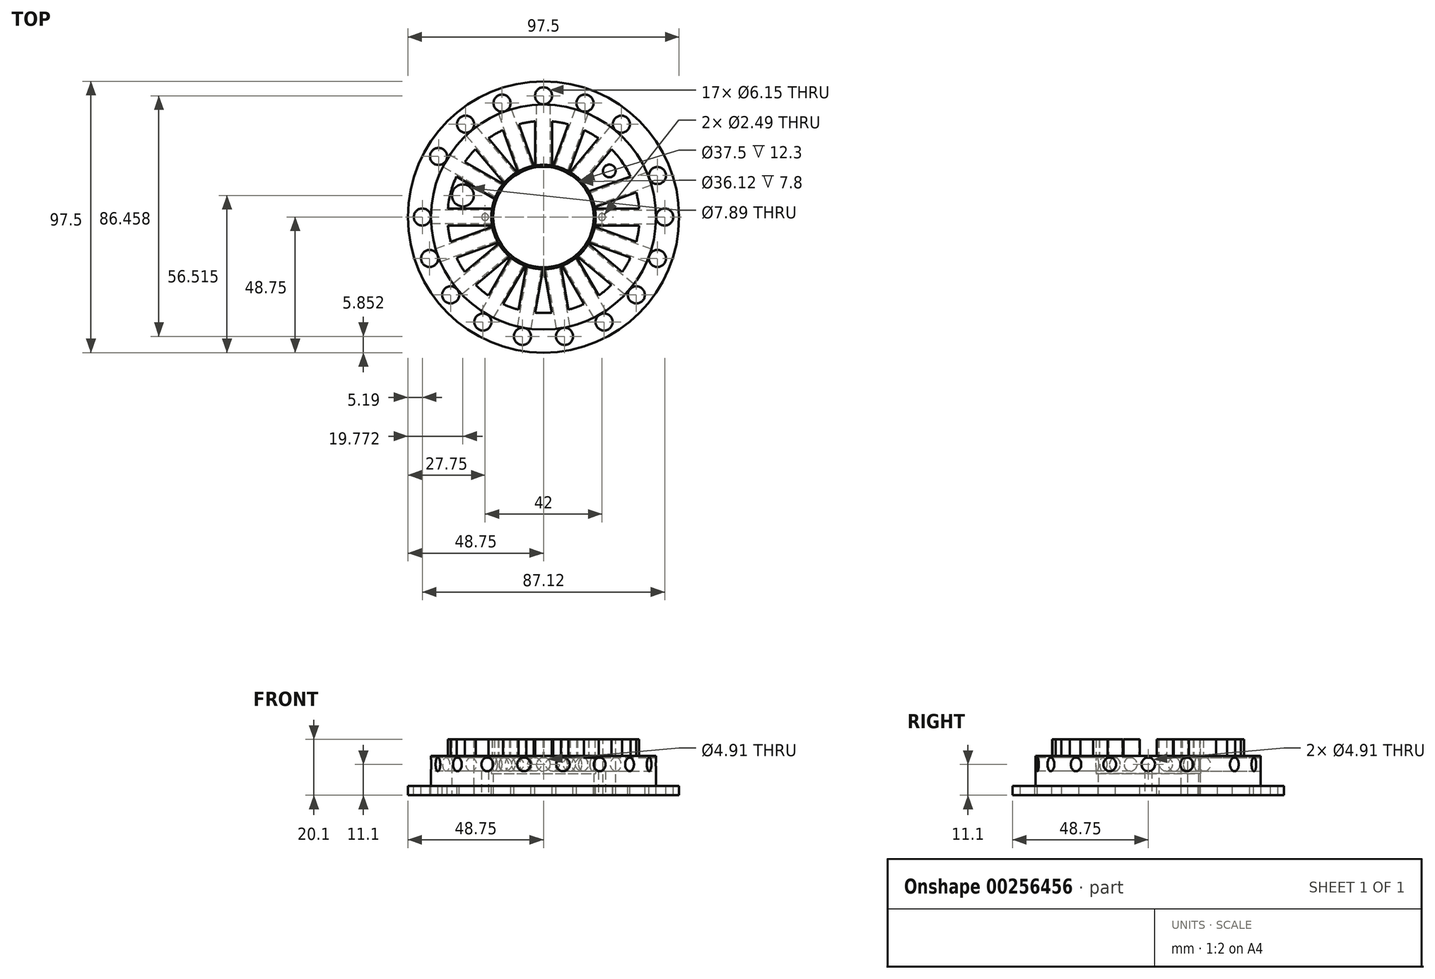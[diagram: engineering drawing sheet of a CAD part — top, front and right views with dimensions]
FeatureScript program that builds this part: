
annotation { "Feature Type Name" : "Feature", "Feature Type Description" : "" }
export const myFeature = defineFeature(function(context is Context, id is Id, definition is map)
    precondition{}
    {
        {
            var Q0;
            Q0=qCreatedBy(makeId("Front.planeOp"),FACE);
            var sketch = newSketch(context, id + "F0", { "sketchPlane" : qUnion([Q0])});
            skLineSegment(sketch, "E0", {"start": v(6.02, 0) * mm, "end": v(16.25, 0) * mm});
            skLineSegment(sketch, "E1", {"start": v(16.25, 0) * mm, "end": v(16.25, 1.1) * mm});
            skLineSegment(sketch, "E2", {"start": v(16.25, 1.1) * mm, "end": v(13.48, 1.1) * mm});
            skLineSegment(sketch, "E3", {"start": v(13.48, 1.1) * mm, "end": v(13.48, 4.7) * mm});
            skLineSegment(sketch, "E4", {"start": v(13.48, 4.7) * mm, "end": v(11.5, 4.7) * mm});
            skLineSegment(sketch, "E5", {"start": v(11.5, 4.7) * mm, "end": v(11.5, 6.7) * mm});
            skLineSegment(sketch, "E6", {"start": v(11.5, 6.7) * mm, "end": v(6.25, 6.7) * mm});
            skLineSegment(sketch, "E7", {"start": v(6.25, 6.7) * mm, "end": v(6.25, 2.6) * mm});
            skLineSegment(sketch, "E8", {"start": v(6.25, 2.6) * mm, "end": v(6.02, 2.6) * mm});
            skLineSegment(sketch, "E9", {"start": v(6.02, 2.6) * mm, "end": v(6.02, 0) * mm});
            skLineSegment(sketch, "E10", {"start": v(0, 0) * mm, "end": v(0, 6.7) * mm, "construction": true});
            skSolve(sketch);
        }
        {
            var Q0;
            Q0=makeQuery(id+"F0.imprint","IMPRINT",FACE,{"disambiguationData":[TD([[makeQuery(id+"F0.imprint","IMPRINT",EDGE,{"derivedFrom":sQuery(id+"F0.wireOp",EDGE,"E0")}),1.0]])]});
            var Q1;
            Q1=sQuery(id+"F0.wireOp",EDGE,"E10");
            revolve(context, id + "F1", {"entities" : qUnion([Q0]), "axis" : qUnion([Q1]), "revolveType" : RevolveType.FULL});
        }
        {
            var Q0;
            Q0=makeQuery(id+"F1.opRevolve","SWEPT_FACE",FACE,{"disambiguationData":[OSD([sQuery(id+"F0.wireOp",EDGE,"E6")])]});
            cPlane(context, id + "F2", {"entities" : qUnion([Q0]), "cplaneType" : CPlaneType.OFFSET, "offset" : 2 * mm, "oppositeDirection" : true, "width" : 150 * mm, "height" : 150 * mm});
        }
        {
            var Q0;
            Q0=qCreatedBy(id+"F2.planeOp",FACE);
            var sketch = newSketch(context, id + "F3", { "sketchPlane" : qUnion([Q0])});
            skLineSegment(sketch, "E11", {"start": v(-15, 1.01) * mm, "end": v(-15, -1.01) * mm});
            skLineSegment(sketch, "E12", {"start": v(-15, -1.01) * mm, "end": v(-5, -1.01) * mm});
            skLineSegment(sketch, "E13", {"start": v(-5, -1.01) * mm, "end": v(-5, 1.01) * mm});
            skLineSegment(sketch, "E14", {"start": v(-5, 1.01) * mm, "end": v(-15, 1.01) * mm});
            skPoint(sketch, "E15.center", {"position": v(0, 0) * mm});
            skLineSegment(sketch, "E16.1.0", {"start": v(-14.44, -4.18) * mm, "end": v(-13.75, -6.08) * mm});
            skLineSegment(sketch, "E16.1.1", {"start": v(-13.75, -6.08) * mm, "end": v(-4.35, -2.66) * mm});
            skLineSegment(sketch, "E16.1.2", {"start": v(-5.05, -0.76) * mm, "end": v(-14.44, -4.18) * mm});
            skLineSegment(sketch, "E16.1.3", {"start": v(-4.35, -2.66) * mm, "end": v(-5.05, -0.76) * mm});
            skLineSegment(sketch, "E16.2.0", {"start": v(-12.14, -8.87) * mm, "end": v(-10.84, -10.42) * mm});
            skLineSegment(sketch, "E16.2.1", {"start": v(-10.84, -10.42) * mm, "end": v(-3.18, -4) * mm});
            skLineSegment(sketch, "E16.2.2", {"start": v(-4.48, -2.44) * mm, "end": v(-12.14, -8.87) * mm});
            skLineSegment(sketch, "E16.2.3", {"start": v(-3.18, -4) * mm, "end": v(-4.48, -2.44) * mm});
            skLineSegment(sketch, "E16.3.0", {"start": v(-8.38, -12.48) * mm, "end": v(-6.62, -13.5) * mm});
            skLineSegment(sketch, "E16.3.1", {"start": v(-6.62, -13.5) * mm, "end": v(-1.62, -4.84) * mm});
            skLineSegment(sketch, "E16.3.2", {"start": v(-3.38, -3.82) * mm, "end": v(-8.38, -12.48) * mm});
            skLineSegment(sketch, "E16.3.3", {"start": v(-1.62, -4.84) * mm, "end": v(-3.38, -3.82) * mm});
            skLineSegment(sketch, "E16.4.0", {"start": v(-3.6, -14.6) * mm, "end": v(-1.6, -14.95) * mm});
            skLineSegment(sketch, "E16.4.1", {"start": v(-1.6, -14.95) * mm, "end": v(0.13, -5.1) * mm});
            skLineSegment(sketch, "E16.4.2", {"start": v(-1.87, -4.75) * mm, "end": v(-3.6, -14.6) * mm});
            skLineSegment(sketch, "E16.4.3", {"start": v(0.13, -5.1) * mm, "end": v(-1.87, -4.75) * mm});
            skLineSegment(sketch, "E16.5.0", {"start": v(1.6, -14.95) * mm, "end": v(3.6, -14.6) * mm});
            skLineSegment(sketch, "E16.5.1", {"start": v(3.6, -14.6) * mm, "end": v(1.87, -4.75) * mm});
            skLineSegment(sketch, "E16.5.2", {"start": v(-0.13, -5.1) * mm, "end": v(1.6, -14.95) * mm});
            skLineSegment(sketch, "E16.5.3", {"start": v(1.87, -4.75) * mm, "end": v(-0.13, -5.1) * mm});
            skLineSegment(sketch, "E16.6.0", {"start": v(6.62, -13.5) * mm, "end": v(8.38, -12.48) * mm});
            skLineSegment(sketch, "E16.6.1", {"start": v(8.38, -12.48) * mm, "end": v(3.38, -3.82) * mm});
            skLineSegment(sketch, "E16.6.2", {"start": v(1.62, -4.84) * mm, "end": v(6.62, -13.5) * mm});
            skLineSegment(sketch, "E16.6.3", {"start": v(3.38, -3.82) * mm, "end": v(1.62, -4.84) * mm});
            skLineSegment(sketch, "E16.7.0", {"start": v(10.84, -10.42) * mm, "end": v(12.14, -8.87) * mm});
            skLineSegment(sketch, "E16.7.1", {"start": v(12.14, -8.87) * mm, "end": v(4.48, -2.44) * mm});
            skLineSegment(sketch, "E16.7.2", {"start": v(3.18, -4) * mm, "end": v(10.84, -10.42) * mm});
            skLineSegment(sketch, "E16.7.3", {"start": v(4.48, -2.44) * mm, "end": v(3.18, -4) * mm});
            skLineSegment(sketch, "E16.8.0", {"start": v(13.75, -6.08) * mm, "end": v(14.44, -4.18) * mm});
            skLineSegment(sketch, "E16.8.1", {"start": v(14.44, -4.18) * mm, "end": v(5.05, -0.76) * mm});
            skLineSegment(sketch, "E16.8.2", {"start": v(4.35, -2.66) * mm, "end": v(13.75, -6.08) * mm});
            skLineSegment(sketch, "E16.8.3", {"start": v(5.05, -0.76) * mm, "end": v(4.35, -2.66) * mm});
            skLineSegment(sketch, "E16.9.0", {"start": v(15, -1.01) * mm, "end": v(15, 1.01) * mm});
            skLineSegment(sketch, "E16.9.1", {"start": v(15, 1.01) * mm, "end": v(5, 1.01) * mm});
            skLineSegment(sketch, "E16.9.2", {"start": v(5, -1.01) * mm, "end": v(15, -1.01) * mm});
            skLineSegment(sketch, "E16.9.3", {"start": v(5, 1.01) * mm, "end": v(5, -1.01) * mm});
            skLineSegment(sketch, "E16.10.0", {"start": v(14.44, 4.18) * mm, "end": v(13.75, 6.08) * mm});
            skLineSegment(sketch, "E16.10.1", {"start": v(13.75, 6.08) * mm, "end": v(4.35, 2.66) * mm});
            skLineSegment(sketch, "E16.10.2", {"start": v(5.05, 0.76) * mm, "end": v(14.44, 4.18) * mm});
            skLineSegment(sketch, "E16.10.3", {"start": v(4.35, 2.66) * mm, "end": v(5.05, 0.76) * mm});
            skLineSegment(sketch, "E16.anchor1", {"start": v(0, 0) * mm, "end": v(-15, -1.01) * mm, "construction": true});
            skLineSegment(sketch, "E16.anchor2", {"start": v(0, 0) * mm, "end": v(13.75, 6.08) * mm, "construction": true});
            skLineSegment(sketch, "E17", {"start": v(-13.5, 6.62) * mm, "end": v(-4.84, 1.62) * mm});
            skLineSegment(sketch, "E18", {"start": v(-4.84, 1.62) * mm, "end": v(-3.82, 3.38) * mm});
            skLineSegment(sketch, "E19", {"start": v(-3.82, 3.38) * mm, "end": v(-12.48, 8.38) * mm});
            skLineSegment(sketch, "E20", {"start": v(-12.48, 8.38) * mm, "end": v(-13.5, 6.62) * mm});
            skLineSegment(sketch, "E21", {"start": v(-13, 7.5) * mm, "end": v(-4.33, 2.5) * mm, "construction": true});
            skLineSegment(sketch, "E22.1.0", {"start": v(-8.87, 12.14) * mm, "end": v(-10.42, 10.84) * mm});
            skLineSegment(sketch, "E22.1.1", {"start": v(-10.42, 10.84) * mm, "end": v(-4, 3.18) * mm});
            skLineSegment(sketch, "E22.1.2", {"start": v(-2.44, 4.48) * mm, "end": v(-8.87, 12.14) * mm});
            skLineSegment(sketch, "E22.1.3", {"start": v(-4, 3.18) * mm, "end": v(-2.44, 4.48) * mm});
            skLineSegment(sketch, "E22.2.0", {"start": v(-4.18, 14.44) * mm, "end": v(-6.08, 13.75) * mm});
            skLineSegment(sketch, "E22.2.1", {"start": v(-6.08, 13.75) * mm, "end": v(-2.66, 4.35) * mm});
            skLineSegment(sketch, "E22.2.2", {"start": v(-0.76, 5.05) * mm, "end": v(-4.18, 14.44) * mm});
            skLineSegment(sketch, "E22.2.3", {"start": v(-2.66, 4.35) * mm, "end": v(-0.76, 5.05) * mm});
            skLineSegment(sketch, "E22.3.0", {"start": v(1.01, 15) * mm, "end": v(-1.01, 15) * mm});
            skLineSegment(sketch, "E22.3.1", {"start": v(-1.01, 15) * mm, "end": v(-1.01, 5) * mm});
            skLineSegment(sketch, "E22.3.2", {"start": v(1.01, 5) * mm, "end": v(1.01, 15) * mm});
            skLineSegment(sketch, "E22.3.3", {"start": v(-1.01, 5) * mm, "end": v(1.01, 5) * mm});
            skLineSegment(sketch, "E22.4.0", {"start": v(6.08, 13.75) * mm, "end": v(4.18, 14.44) * mm});
            skLineSegment(sketch, "E22.4.1", {"start": v(4.18, 14.44) * mm, "end": v(0.76, 5.05) * mm});
            skLineSegment(sketch, "E22.4.2", {"start": v(2.66, 4.35) * mm, "end": v(6.08, 13.75) * mm});
            skLineSegment(sketch, "E22.4.3", {"start": v(0.76, 5.05) * mm, "end": v(2.66, 4.35) * mm});
            skLineSegment(sketch, "E22.5.0", {"start": v(10.42, 10.84) * mm, "end": v(8.87, 12.14) * mm});
            skLineSegment(sketch, "E22.5.1", {"start": v(8.87, 12.14) * mm, "end": v(2.44, 4.48) * mm});
            skLineSegment(sketch, "E22.5.2", {"start": v(4, 3.18) * mm, "end": v(10.42, 10.84) * mm});
            skLineSegment(sketch, "E22.5.3", {"start": v(2.44, 4.48) * mm, "end": v(4, 3.18) * mm});
            skLineSegment(sketch, "E22.anchor1", {"start": v(0, 0) * mm, "end": v(-13.5, 6.62) * mm, "construction": true});
            skLineSegment(sketch, "E22.anchor2", {"start": v(0, 0) * mm, "end": v(8.87, 12.14) * mm, "construction": true});
            skSolve(sketch);
        }
        {
            var Q0;
            Q0=qSketchRegion(id+"F3",true);
            extrude(context, id + "F4", {"entities" : qUnion([Q0]), "operationType" : NewBodyOperationType.REMOVE, "endBound" : BoundingType.THROUGH_ALL, "depth" : 25 * mm});
        }
        {
            var Q0;
            Q0=makeQuery(id+"F1.opRevolve","SWEPT_FACE",FACE,{"disambiguationData":[OSD([sQuery(id+"F0.wireOp",EDGE,"E2")])]});
            var sketch = newSketch(context, id + "F5", { "sketchPlane" : qUnion([Q0])});
            skCircle(sketch, "E23", {"center": v(0, 0) * mm, "radius": 14.52 * mm, "construction": true});
            skCircle(sketch, "E24", {"center": v(-14.52, 0) * mm, "radius": 1.02 * mm});
            skLineSegment(sketch, "E25.anchor1", {"start": v(0, 0) * mm, "end": v(-14.52, 0) * mm, "construction": true});
            skCircle(sketch, "E26.1.0", {"center": v(-12.57, 7.26) * mm, "radius": 1.02 * mm});
            skLineSegment(sketch, "E26.anchor2", {"start": v(0, 0) * mm, "end": v(-12.57, 7.26) * mm, "construction": true});
            skCircle(sketch, "E27.1.0", {"center": v(-13.64, -4.97) * mm, "radius": 1.02 * mm});
            skCircle(sketch, "E27.2.0", {"center": v(-11.12, -9.33) * mm, "radius": 1.02 * mm});
            skCircle(sketch, "E27.3.0", {"center": v(-7.26, -12.57) * mm, "radius": 1.02 * mm});
            skCircle(sketch, "E27.4.0", {"center": v(-2.52, -14.3) * mm, "radius": 1.02 * mm});
            skCircle(sketch, "E27.5.0", {"center": v(2.52, -14.3) * mm, "radius": 1.02 * mm});
            skCircle(sketch, "E27.6.0", {"center": v(7.26, -12.57) * mm, "radius": 1.02 * mm});
            skCircle(sketch, "E27.7.0", {"center": v(11.12, -9.33) * mm, "radius": 1.02 * mm});
            skCircle(sketch, "E27.8.0", {"center": v(13.64, -4.97) * mm, "radius": 1.02 * mm});
            skCircle(sketch, "E27.9.0", {"center": v(14.52, 0) * mm, "radius": 1.02 * mm});
            skCircle(sketch, "E27.10.0", {"center": v(13.64, 4.97) * mm, "radius": 1.02 * mm});
            skLineSegment(sketch, "E27.anchor2", {"start": v(0, 0) * mm, "end": v(13.64, 4.97) * mm, "construction": true});
            skCircle(sketch, "E28.1.0", {"center": v(-9.33, 11.12) * mm, "radius": 1.02 * mm});
            skCircle(sketch, "E28.2.0", {"center": v(-4.97, 13.64) * mm, "radius": 1.02 * mm});
            skCircle(sketch, "E28.3.0", {"center": v(0, 14.52) * mm, "radius": 1.02 * mm});
            skCircle(sketch, "E28.4.0", {"center": v(4.97, 13.64) * mm, "radius": 1.02 * mm});
            skCircle(sketch, "E28.5.0", {"center": v(9.33, 11.12) * mm, "radius": 1.02 * mm});
            skLineSegment(sketch, "E28.anchor2", {"start": v(0, 0) * mm, "end": v(9.33, 11.12) * mm, "construction": true});
            skSolve(sketch);
        }
        {
            var Q0;
            Q0=qSketchRegion(id+"F5",true);
            extrude(context, id + "F6", {"entities" : qUnion([Q0]), "operationType" : NewBodyOperationType.REMOVE, "endBound" : BoundingType.THROUGH_ALL, "oppositeDirection" : true, "depth" : 25 * mm});
        }
        {
            var Q0;
            Q0=makeQuery(id+"F1.opRevolve","SWEPT_FACE",FACE,{"disambiguationData":[OSD([sQuery(id+"F0.wireOp",EDGE,"E0")])]});
            var sketch = newSketch(context, id + "F7", { "sketchPlane" : qUnion([Q0])});
            skCircle(sketch, "E29", {"center": v(-9.66, -2.59) * mm, "radius": 1.31 * mm});
            skLineSegment(sketch, "E30", {"start": v(-9.66, -2.59) * mm, "end": v(0, 0) * mm, "construction": true});
            skSolve(sketch);
        }
        {
            var Q0;
            Q0=makeQuery(id+"F7.imprint","IMPRINT",FACE,{"disambiguationData":[TD([[makeQuery(id+"F7.imprint","IMPRINT",EDGE,{"derivedFrom":sQuery(id+"F7.wireOp",EDGE,"E29")}),1.0]])]});
            extrude(context, id + "F8", {"entities" : qUnion([Q0]), "operationType" : NewBodyOperationType.REMOVE, "endBound" : BoundingType.THROUGH_ALL, "oppositeDirection" : true, "depth" : 25 * mm});
        }
        {
            var Q0;
            Q0=makeQuery(id+"F4.boolean.opBoolean","SPLIT",FACE,{"disambiguationData":[TD([makeQuery(id+"F4.opExtrude","SWEPT_FACE",FACE,{"disambiguationData":[OSD([sQuery(id+"F3.wireOp",EDGE,"E16.10.2")])]})])],"derivedFrom":makeQuery(id+"F1.opRevolve","SWEPT_FACE",FACE,{"disambiguationData":[OSD([sQuery(id+"F0.wireOp",EDGE,"E6")])]})});
            var sketch = newSketch(context, id + "F9", { "sketchPlane" : qUnion([Q0])});
            skCircle(sketch, "E31", {"center": v(7.88, 5.52) * mm, "radius": 0.76 * mm});
            skLineSegment(sketch, "E32", {"start": v(7.88, 5.52) * mm, "end": v(0, 0) * mm, "construction": true});
            skSolve(sketch);
        }
        {
            var Q0;
            Q0=makeQuery(id+"F9.imprint","IMPRINT",FACE,{"disambiguationData":[TD([[makeQuery(id+"F9.imprint","IMPRINT",EDGE,{"derivedFrom":sQuery(id+"F9.wireOp",EDGE,"E31")}),1.0]])]});
            var Q2;
            Q2=makeQuery(id+"F1.opRevolve","SWEPT_FACE",FACE,{"disambiguationData":[OSD([sQuery(id+"F0.wireOp",EDGE,"E0")])]});
            extrude(context, id + "F10", {"entities" : qUnion([Q0]), "operationType" : NewBodyOperationType.REMOVE, "endBound" : BoundingType.UP_TO_SURFACE, "oppositeDirection" : true, "depth" : 1.3 * mm, "endBoundEntityFace" : qUnion([Q2])});
        }
        {
            var Q0;
            Q0=makeQuery(id+"F1.opRevolve","SWEPT_FACE",FACE,{"disambiguationData":[OSD([sQuery(id+"F0.wireOp",EDGE,"E0")])]});
            var sketch = newSketch(context, id + "F11", { "sketchPlane" : qUnion([Q0])});
            skCircle(sketch, "E33", {"center": v(0, 0) * mm, "radius": 7 * mm, "construction": true});
            skCircle(sketch, "E34", {"center": v(-7, 0) * mm, "radius": 0.41 * mm});
            skCircle(sketch, "E35", {"center": v(7, 0) * mm, "radius": 0.41 * mm});
            skSolve(sketch);
        }
        {
            var Q0;
            {Q0=qUnion([makeQuery(id+"F11.imprint","IMPRINT",FACE,{"disambiguationData":[TD([[makeQuery(id+"F11.imprint","IMPRINT",EDGE,{"derivedFrom":sQuery(id+"F11.wireOp",EDGE,"E34")}),1.0]])]}),makeQuery(id+"F11.imprint","IMPRINT",FACE,{"disambiguationData":[TD([[makeQuery(id+"F11.imprint","IMPRINT",EDGE,{"derivedFrom":sQuery(id+"F11.wireOp",EDGE,"E35")}),1.0]])]})]);}
            extrude(context, id + "F12", {"entities" : qUnion([Q0]), "operationType" : NewBodyOperationType.REMOVE, "oppositeDirection" : true, "depth" : 3.7 * mm});
        }
        {
            var Q0;
            Q0=qCreatedBy(id+"F2.planeOp",FACE);
            cPlane(context, id + "F13", {"entities" : qUnion([Q0]), "cplaneType" : CPlaneType.OFFSET, "offset" : 1 * mm, "oppositeDirection" : true, "width" : 150 * mm, "height" : 150 * mm});
        }
        {
            var Q0;
            Q0=qCreatedBy(id+"F13.planeOp",FACE);
            var sketch = newSketch(context, id + "F14", { "sketchPlane" : qUnion([Q0])});
            skLineSegment(sketch, "E36.bottom", {"start": v(-17.2, 0.82) * mm, "end": v(-6.2, 0.82) * mm});
            skLineSegment(sketch, "E36.top", {"start": v(-17.2, 0) * mm, "end": v(-6.2, 0) * mm});
            skLineSegment(sketch, "E36.left", {"start": v(-17.2, 0.82) * mm, "end": v(-17.2, 0) * mm});
            skLineSegment(sketch, "E36.right", {"start": v(-6.2, 0.82) * mm, "end": v(-6.2, 0) * mm});
            skSolve(sketch);
        }
        {
            var Q0;
            Q0=makeQuery(id+"F14.imprint","IMPRINT",FACE,{"disambiguationData":[TD([[makeQuery(id+"F14.imprint","IMPRINT",EDGE,{"derivedFrom":sQuery(id+"F14.wireOp",EDGE,"E36.bottom")}),-1.0]])]});
            var Q1;
            Q1=sQuery(id+"F14.wireOp",EDGE,"E36.top");
            revolve(context, id + "F15", {"entities" : qUnion([Q0]), "axis" : qUnion([Q1]), "revolveType" : RevolveType.FULL});
        }
        {
            var Q0;
            Q0=makeQuery(id+"F15.opRevolve","SWEPT_BODY",BODY,{"disambiguationData":[OSD([sQuery(id+"F14.wireOp",EDGE,"E36.bottom"),sQuery(id+"F14.wireOp",EDGE,"E36.top"),sQuery(id+"F14.wireOp",EDGE,"E36.left"),sQuery(id+"F14.wireOp",EDGE,"E36.right")])]});
            var Q1;
            Q1=sQuery(id+"F0.wireOp",EDGE,"E10");
            circularPattern(context, id + "F16", {"entities" : qUnion([Q0]), "axis" : qUnion([Q1]), "angle" : 20 * degree, "instanceCount" : round(11), "computeTransformsWithoutBuiltin" : true});
        }
        {
            var Q0;
            Q0=makeQuery(id+"F15.opRevolve","SWEPT_BODY",BODY,{"disambiguationData":[OSD([sQuery(id+"F14.wireOp",EDGE,"E36.bottom"),sQuery(id+"F14.wireOp",EDGE,"E36.top"),sQuery(id+"F14.wireOp",EDGE,"E36.left"),sQuery(id+"F14.wireOp",EDGE,"E36.right")])]});
            var Q1;
            Q1=sQuery(id+"F0.wireOp",EDGE,"E10");
            transform(context, id + "F17", {"entities" : qUnion([Q0]), "transformType" : TransformType.ROTATION, "transformAxis" : qUnion([Q1]), "angle" : 30 * degree, "oppositeDirection" : true, "makeCopy" : true});
        }
        {
            var Q0;
            Q0=makeQuery(id+"F17.opPattern","COPY",FACE,{"derivedFrom":makeQuery(id+"F15.opRevolve","SWEPT_FACE",FACE,{"disambiguationData":[OSD([sQuery(id+"F14.wireOp",EDGE,"E36.bottom")])]}),"instanceName":"1"});
            var Q1;
            Q1=makeQuery(id+"F17.opPattern","COPY",BODY,{"derivedFrom":makeQuery(id+"F15.opRevolve","SWEPT_BODY",BODY,{"disambiguationData":[OSD([sQuery(id+"F14.wireOp",EDGE,"E36.bottom"),sQuery(id+"F14.wireOp",EDGE,"E36.top"),sQuery(id+"F14.wireOp",EDGE,"E36.left"),sQuery(id+"F14.wireOp",EDGE,"E36.right")])]}),"instanceName":"1"});
            var Q2;
            Q2=sQuery(id+"F0.wireOp",EDGE,"E10");
            circularPattern(context, id + "F18", {"entities" : qUnion([Q1]), "axis" : qUnion([Q2]), "angle" : 20 * degree, "instanceCount" : round(6), "oppositeDirection" : true, "computeTransformsWithoutBuiltin" : true});
        }
        {
            var Q0;
            Q0=makeQuery(id+"F15.opRevolve","SWEPT_BODY",BODY,{"disambiguationData":[OSD([sQuery(id+"F14.wireOp",EDGE,"E36.bottom"),sQuery(id+"F14.wireOp",EDGE,"E36.top"),sQuery(id+"F14.wireOp",EDGE,"E36.left"),sQuery(id+"F14.wireOp",EDGE,"E36.right")])]});
            var Q1;
            Q1=makeQuery(id+"F16.opPattern","COPY",BODY,{"derivedFrom":makeQuery(id+"F15.opRevolve","SWEPT_BODY",BODY,{"disambiguationData":[OSD([sQuery(id+"F14.wireOp",EDGE,"E36.bottom"),sQuery(id+"F14.wireOp",EDGE,"E36.top"),sQuery(id+"F14.wireOp",EDGE,"E36.left"),sQuery(id+"F14.wireOp",EDGE,"E36.right")])]}),"instanceName":"1"});
            var Q2;
            Q2=makeQuery(id+"F16.opPattern","COPY",BODY,{"derivedFrom":makeQuery(id+"F15.opRevolve","SWEPT_BODY",BODY,{"disambiguationData":[OSD([sQuery(id+"F14.wireOp",EDGE,"E36.bottom"),sQuery(id+"F14.wireOp",EDGE,"E36.top"),sQuery(id+"F14.wireOp",EDGE,"E36.left"),sQuery(id+"F14.wireOp",EDGE,"E36.right")])]}),"instanceName":"2"});
            var Q3;
            Q3=makeQuery(id+"F16.opPattern","COPY",BODY,{"derivedFrom":makeQuery(id+"F15.opRevolve","SWEPT_BODY",BODY,{"disambiguationData":[OSD([sQuery(id+"F14.wireOp",EDGE,"E36.bottom"),sQuery(id+"F14.wireOp",EDGE,"E36.top"),sQuery(id+"F14.wireOp",EDGE,"E36.left"),sQuery(id+"F14.wireOp",EDGE,"E36.right")])]}),"instanceName":"3"});
            var Q4;
            Q4=makeQuery(id+"F16.opPattern","COPY",BODY,{"derivedFrom":makeQuery(id+"F15.opRevolve","SWEPT_BODY",BODY,{"disambiguationData":[OSD([sQuery(id+"F14.wireOp",EDGE,"E36.bottom"),sQuery(id+"F14.wireOp",EDGE,"E36.top"),sQuery(id+"F14.wireOp",EDGE,"E36.left"),sQuery(id+"F14.wireOp",EDGE,"E36.right")])]}),"instanceName":"4"});
            var Q5;
            Q5=makeQuery(id+"F16.opPattern","COPY",BODY,{"derivedFrom":makeQuery(id+"F15.opRevolve","SWEPT_BODY",BODY,{"disambiguationData":[OSD([sQuery(id+"F14.wireOp",EDGE,"E36.bottom"),sQuery(id+"F14.wireOp",EDGE,"E36.top"),sQuery(id+"F14.wireOp",EDGE,"E36.left"),sQuery(id+"F14.wireOp",EDGE,"E36.right")])]}),"instanceName":"5"});
            var Q6;
            Q6=makeQuery(id+"F16.opPattern","COPY",BODY,{"derivedFrom":makeQuery(id+"F15.opRevolve","SWEPT_BODY",BODY,{"disambiguationData":[OSD([sQuery(id+"F14.wireOp",EDGE,"E36.bottom"),sQuery(id+"F14.wireOp",EDGE,"E36.top"),sQuery(id+"F14.wireOp",EDGE,"E36.left"),sQuery(id+"F14.wireOp",EDGE,"E36.right")])]}),"instanceName":"6"});
            var Q7;
            Q7=makeQuery(id+"F16.opPattern","COPY",BODY,{"derivedFrom":makeQuery(id+"F15.opRevolve","SWEPT_BODY",BODY,{"disambiguationData":[OSD([sQuery(id+"F14.wireOp",EDGE,"E36.bottom"),sQuery(id+"F14.wireOp",EDGE,"E36.top"),sQuery(id+"F14.wireOp",EDGE,"E36.left"),sQuery(id+"F14.wireOp",EDGE,"E36.right")])]}),"instanceName":"7"});
            var Q8;
            Q8=makeQuery(id+"F16.opPattern","COPY",BODY,{"derivedFrom":makeQuery(id+"F15.opRevolve","SWEPT_BODY",BODY,{"disambiguationData":[OSD([sQuery(id+"F14.wireOp",EDGE,"E36.bottom"),sQuery(id+"F14.wireOp",EDGE,"E36.top"),sQuery(id+"F14.wireOp",EDGE,"E36.left"),sQuery(id+"F14.wireOp",EDGE,"E36.right")])]}),"instanceName":"8"});
            var Q9;
            Q9=makeQuery(id+"F16.opPattern","COPY",BODY,{"derivedFrom":makeQuery(id+"F15.opRevolve","SWEPT_BODY",BODY,{"disambiguationData":[OSD([sQuery(id+"F14.wireOp",EDGE,"E36.bottom"),sQuery(id+"F14.wireOp",EDGE,"E36.top"),sQuery(id+"F14.wireOp",EDGE,"E36.left"),sQuery(id+"F14.wireOp",EDGE,"E36.right")])]}),"instanceName":"9"});
            var Q10;
            Q10=makeQuery(id+"F16.opPattern","COPY",BODY,{"derivedFrom":makeQuery(id+"F15.opRevolve","SWEPT_BODY",BODY,{"disambiguationData":[OSD([sQuery(id+"F14.wireOp",EDGE,"E36.bottom"),sQuery(id+"F14.wireOp",EDGE,"E36.top"),sQuery(id+"F14.wireOp",EDGE,"E36.left"),sQuery(id+"F14.wireOp",EDGE,"E36.right")])]}),"instanceName":"10"});
            var Q11;
            Q11=makeQuery(id+"F17.opPattern","COPY",BODY,{"derivedFrom":makeQuery(id+"F15.opRevolve","SWEPT_BODY",BODY,{"disambiguationData":[OSD([sQuery(id+"F14.wireOp",EDGE,"E36.bottom"),sQuery(id+"F14.wireOp",EDGE,"E36.top"),sQuery(id+"F14.wireOp",EDGE,"E36.left"),sQuery(id+"F14.wireOp",EDGE,"E36.right")])]}),"instanceName":"1"});
            var Q12;
            Q12=makeQuery(id+"F18.opPattern","COPY",BODY,{"derivedFrom":makeQuery(id+"F17.opPattern","COPY",BODY,{"derivedFrom":makeQuery(id+"F15.opRevolve","SWEPT_BODY",BODY,{"disambiguationData":[OSD([sQuery(id+"F14.wireOp",EDGE,"E36.bottom"),sQuery(id+"F14.wireOp",EDGE,"E36.top"),sQuery(id+"F14.wireOp",EDGE,"E36.left"),sQuery(id+"F14.wireOp",EDGE,"E36.right")])]}),"instanceName":"1"}),"instanceName":"1"});
            var Q13;
            Q13=makeQuery(id+"F18.opPattern","COPY",BODY,{"derivedFrom":makeQuery(id+"F17.opPattern","COPY",BODY,{"derivedFrom":makeQuery(id+"F15.opRevolve","SWEPT_BODY",BODY,{"disambiguationData":[OSD([sQuery(id+"F14.wireOp",EDGE,"E36.bottom"),sQuery(id+"F14.wireOp",EDGE,"E36.top"),sQuery(id+"F14.wireOp",EDGE,"E36.left"),sQuery(id+"F14.wireOp",EDGE,"E36.right")])]}),"instanceName":"1"}),"instanceName":"2"});
            var Q14;
            Q14=makeQuery(id+"F18.opPattern","COPY",BODY,{"derivedFrom":makeQuery(id+"F17.opPattern","COPY",BODY,{"derivedFrom":makeQuery(id+"F15.opRevolve","SWEPT_BODY",BODY,{"disambiguationData":[OSD([sQuery(id+"F14.wireOp",EDGE,"E36.bottom"),sQuery(id+"F14.wireOp",EDGE,"E36.top"),sQuery(id+"F14.wireOp",EDGE,"E36.left"),sQuery(id+"F14.wireOp",EDGE,"E36.right")])]}),"instanceName":"1"}),"instanceName":"3"});
            var Q15;
            Q15=makeQuery(id+"F18.opPattern","COPY",BODY,{"derivedFrom":makeQuery(id+"F17.opPattern","COPY",BODY,{"derivedFrom":makeQuery(id+"F15.opRevolve","SWEPT_BODY",BODY,{"disambiguationData":[OSD([sQuery(id+"F14.wireOp",EDGE,"E36.bottom"),sQuery(id+"F14.wireOp",EDGE,"E36.top"),sQuery(id+"F14.wireOp",EDGE,"E36.left"),sQuery(id+"F14.wireOp",EDGE,"E36.right")])]}),"instanceName":"1"}),"instanceName":"4"});
            var Q16;
            Q16=makeQuery(id+"F18.opPattern","COPY",BODY,{"derivedFrom":makeQuery(id+"F17.opPattern","COPY",BODY,{"derivedFrom":makeQuery(id+"F15.opRevolve","SWEPT_BODY",BODY,{"disambiguationData":[OSD([sQuery(id+"F14.wireOp",EDGE,"E36.bottom"),sQuery(id+"F14.wireOp",EDGE,"E36.top"),sQuery(id+"F14.wireOp",EDGE,"E36.left"),sQuery(id+"F14.wireOp",EDGE,"E36.right")])]}),"instanceName":"1"}),"instanceName":"5"});
            var Q17;
            Q17=makeQuery(id+"F1.opRevolve","SWEPT_BODY",BODY,{"disambiguationData":[OSD([sQuery(id+"F0.wireOp",EDGE,"E0"),sQuery(id+"F0.wireOp",EDGE,"E1"),sQuery(id+"F0.wireOp",EDGE,"E2"),sQuery(id+"F0.wireOp",EDGE,"E3"),sQuery(id+"F0.wireOp",EDGE,"E4"),sQuery(id+"F0.wireOp",EDGE,"E5"),sQuery(id+"F0.wireOp",EDGE,"E6"),sQuery(id+"F0.wireOp",EDGE,"E7"),sQuery(id+"F0.wireOp",EDGE,"E8"),sQuery(id+"F0.wireOp",EDGE,"E9")])]});
            booleanBodies(context, id + "F19", {"operationType" : BooleanOperationType.SUBTRACTION, "tools" : qUnion([Q0, Q1, Q2, Q3, Q4, Q5, Q6, Q7, Q8, Q9, Q10, Q11, Q12, Q13, Q14, Q15, Q16]), "targets" : qUnion([Q17])});
        }
        {
            var Q0;
            Q0=makeQuery(id+"F4.boolean.opBoolean","MERGE",FACE,{"derivedFrom":[makeQuery(id+"F1.opRevolve","SWEPT_FACE",FACE,{"disambiguationData":[OSD([sQuery(id+"F0.wireOp",EDGE,"E4")])]}),makeQuery(id+"F4.opExtrude","CAP_FACE",FACE,{"disambiguationData":[OSD([sQuery(id+"F3.wireOp",EDGE,"E11"),sQuery(id+"F3.wireOp",EDGE,"E12"),sQuery(id+"F3.wireOp",EDGE,"E13"),sQuery(id+"F3.wireOp",EDGE,"E14"),sQuery(id+"F3.wireOp",EDGE,"E16.1.0"),sQuery(id+"F3.wireOp",EDGE,"E16.1.1"),sQuery(id+"F3.wireOp",EDGE,"E16.1.2"),sQuery(id+"F3.wireOp",EDGE,"E16.1.3"),sQuery(id+"F3.wireOp",EDGE,"E16.2.0"),sQuery(id+"F3.wireOp",EDGE,"E16.2.1"),sQuery(id+"F3.wireOp",EDGE,"E16.2.2"),sQuery(id+"F3.wireOp",EDGE,"E16.2.3"),sQuery(id+"F3.wireOp",EDGE,"E16.3.0"),sQuery(id+"F3.wireOp",EDGE,"E16.3.1"),sQuery(id+"F3.wireOp",EDGE,"E16.3.2"),sQuery(id+"F3.wireOp",EDGE,"E16.3.3"),sQuery(id+"F3.wireOp",EDGE,"E16.4.0"),sQuery(id+"F3.wireOp",EDGE,"E16.4.1"),sQuery(id+"F3.wireOp",EDGE,"E16.4.2"),sQuery(id+"F3.wireOp",EDGE,"E16.4.3"),sQuery(id+"F3.wireOp",EDGE,"E16.5.0"),sQuery(id+"F3.wireOp",EDGE,"E16.5.1"),sQuery(id+"F3.wireOp",EDGE,"E16.5.2"),sQuery(id+"F3.wireOp",EDGE,"E16.5.3"),sQuery(id+"F3.wireOp",EDGE,"E16.6.0"),sQuery(id+"F3.wireOp",EDGE,"E16.6.1"),sQuery(id+"F3.wireOp",EDGE,"E16.6.2"),sQuery(id+"F3.wireOp",EDGE,"E16.6.3"),sQuery(id+"F3.wireOp",EDGE,"E16.7.0"),sQuery(id+"F3.wireOp",EDGE,"E16.7.1"),sQuery(id+"F3.wireOp",EDGE,"E16.7.2"),sQuery(id+"F3.wireOp",EDGE,"E16.7.3"),sQuery(id+"F3.wireOp",EDGE,"E16.8.0"),sQuery(id+"F3.wireOp",EDGE,"E16.8.1"),sQuery(id+"F3.wireOp",EDGE,"E16.8.2"),sQuery(id+"F3.wireOp",EDGE,"E16.8.3"),sQuery(id+"F3.wireOp",EDGE,"E16.9.0"),sQuery(id+"F3.wireOp",EDGE,"E16.9.1"),sQuery(id+"F3.wireOp",EDGE,"E16.9.2"),sQuery(id+"F3.wireOp",EDGE,"E16.9.3"),sQuery(id+"F3.wireOp",EDGE,"E16.10.0"),sQuery(id+"F3.wireOp",EDGE,"E16.10.1"),sQuery(id+"F3.wireOp",EDGE,"E16.10.2"),sQuery(id+"F3.wireOp",EDGE,"E16.10.3")])],"isStart":true}),makeQuery(id+"F4.opExtrude","CAP_FACE",FACE,{"disambiguationData":[OSD([sQuery(id+"F3.wireOp",EDGE,"E17"),sQuery(id+"F3.wireOp",EDGE,"E18"),sQuery(id+"F3.wireOp",EDGE,"E19"),sQuery(id+"F3.wireOp",EDGE,"E20"),sQuery(id+"F3.wireOp",EDGE,"E22.1.0"),sQuery(id+"F3.wireOp",EDGE,"E22.1.1"),sQuery(id+"F3.wireOp",EDGE,"E22.1.2"),sQuery(id+"F3.wireOp",EDGE,"E22.1.3"),sQuery(id+"F3.wireOp",EDGE,"E22.2.0"),sQuery(id+"F3.wireOp",EDGE,"E22.2.1"),sQuery(id+"F3.wireOp",EDGE,"E22.2.2"),sQuery(id+"F3.wireOp",EDGE,"E22.2.3"),sQuery(id+"F3.wireOp",EDGE,"E22.3.0"),sQuery(id+"F3.wireOp",EDGE,"E22.3.1"),sQuery(id+"F3.wireOp",EDGE,"E22.3.2"),sQuery(id+"F3.wireOp",EDGE,"E22.3.3"),sQuery(id+"F3.wireOp",EDGE,"E22.4.0"),sQuery(id+"F3.wireOp",EDGE,"E22.4.1"),sQuery(id+"F3.wireOp",EDGE,"E22.4.2"),sQuery(id+"F3.wireOp",EDGE,"E22.4.3"),sQuery(id+"F3.wireOp",EDGE,"E22.5.0"),sQuery(id+"F3.wireOp",EDGE,"E22.5.1"),sQuery(id+"F3.wireOp",EDGE,"E22.5.2"),sQuery(id+"F3.wireOp",EDGE,"E22.5.3")])],"isStart":true})]});
            cPlane(context, id + "F20", {"entities" : qUnion([Q0]), "cplaneType" : CPlaneType.OFFSET, "offset" : 4 * mm, "oppositeDirection" : true, "width" : 150 * mm, "height" : 150 * mm});
        }
        {
            var Q0;
            Q0=qCreatedBy(id+"F20.planeOp",FACE);
            var sketch = newSketch(context, id + "F21", { "sketchPlane" : qUnion([Q0])});
            skCircle(sketch, "E37", {"center": v(0, 0) * mm, "radius": 24.5 * mm});
            skCircle(sketch, "E38", {"center": v(0, 0) * mm, "radius": 23.9 * mm});
            skSolve(sketch);
        }
        {
            var Q0;
            Q0=makeQuery(id+"F21.imprint","IMPRINT",FACE,{"disambiguationData":[TD([[makeQuery(id+"F21.imprint","IMPRINT",EDGE,{"derivedFrom":sQuery(id+"F21.wireOp",EDGE,"E37")}),1.0]])]});
            extrude(context, id + "F22", {"entities" : qUnion([Q0]), "operationType" : NewBodyOperationType.REMOVE, "depth" : 0.7 * mm});
        }
        {
            var Q0;
            Q0=makeQuery(id+"F1.opRevolve","SWEPT_BODY",BODY,{"disambiguationData":[OSD([sQuery(id+"F0.wireOp",EDGE,"E0"),sQuery(id+"F0.wireOp",EDGE,"E1"),sQuery(id+"F0.wireOp",EDGE,"E2"),sQuery(id+"F0.wireOp",EDGE,"E3"),sQuery(id+"F0.wireOp",EDGE,"E4"),sQuery(id+"F0.wireOp",EDGE,"E5"),sQuery(id+"F0.wireOp",EDGE,"E6"),sQuery(id+"F0.wireOp",EDGE,"E7"),sQuery(id+"F0.wireOp",EDGE,"E8"),sQuery(id+"F0.wireOp",EDGE,"E9")])]});
            var Q1;
            Q1=qCreatedBy(makeId("Origin.pointOp"),VERTEX);
            transform(context, id + "F23", {"entities" : qUnion([Q0]), "transformType" : TransformType.SCALE_UNIFORMLY, "scale" : 3, "makeCopy" : false, "scalePoint" : qUnion([Q1])});
        }
    });
